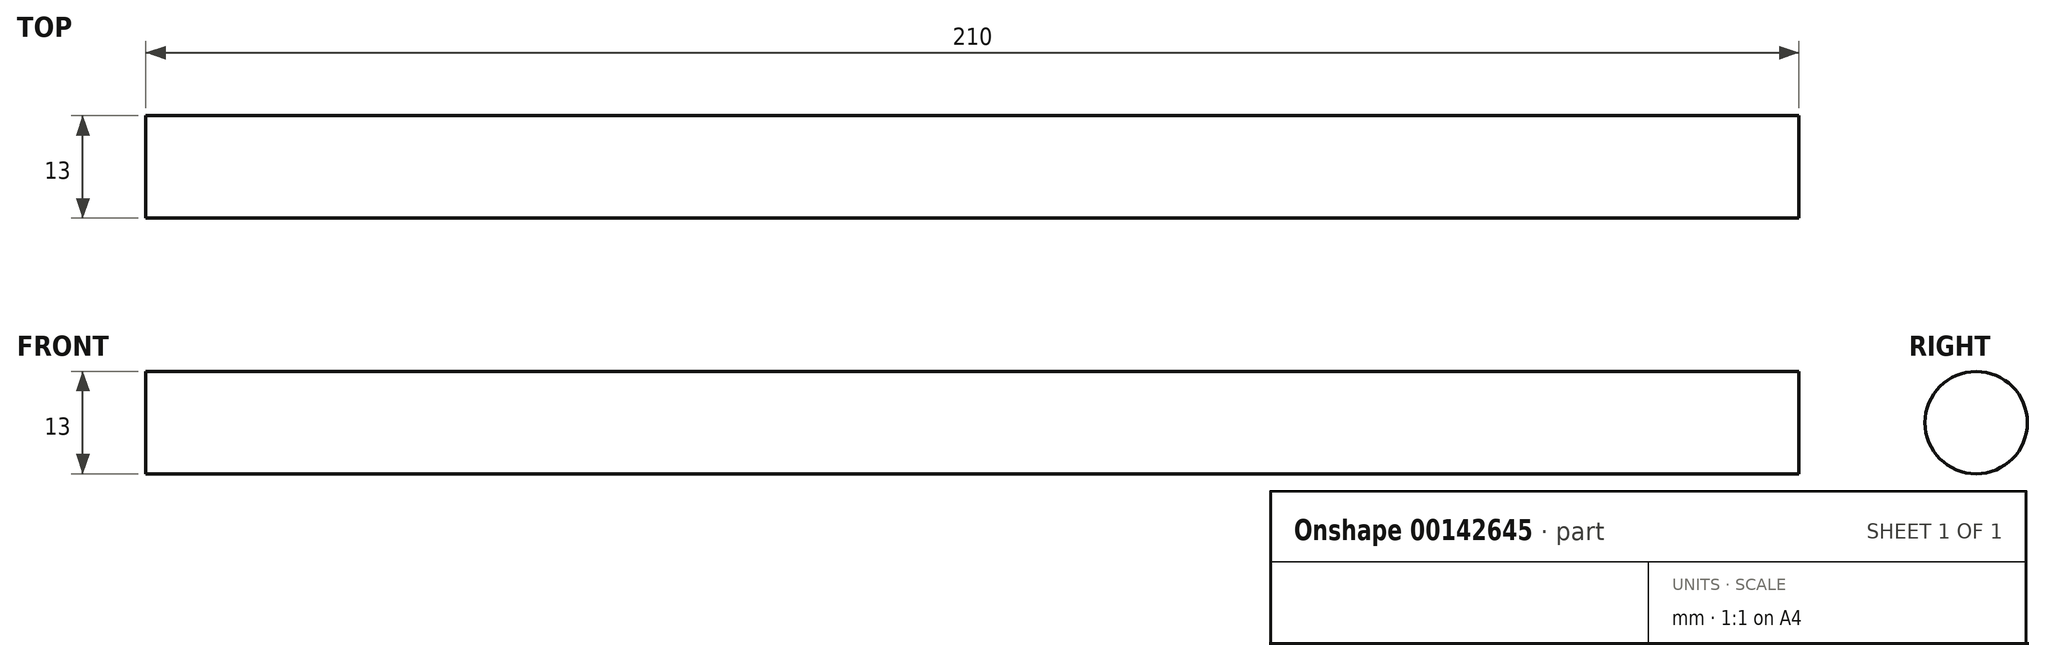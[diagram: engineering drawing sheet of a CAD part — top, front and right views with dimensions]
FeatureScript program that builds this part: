
annotation { "Feature Type Name" : "Feature", "Feature Type Description" : "" }
export const myFeature = defineFeature(function(context is Context, id is Id, definition is map)
    precondition{}
    {
        {
            var Q0;
            Q0=qCreatedBy(makeId("Right.planeOp"),FACE);
            var sketch = newSketch(context, id + "F0", { "sketchPlane" : qUnion([Q0])});
            skCircle(sketch, "E0", {"center": v(0, 0) * mm, "radius": 6.5 * mm});
            skSolve(sketch);
        }
        {
            var Q0;
            Q0 = qSketchRegion(id + "F0", true);
            extrude(context, id + "F1", {"entities" : qUnion([Q0]), "endBound" : BoundingType.SYMMETRIC, "oppositeDirection" : true, "depth" : 210 * mm});
        }
    });
